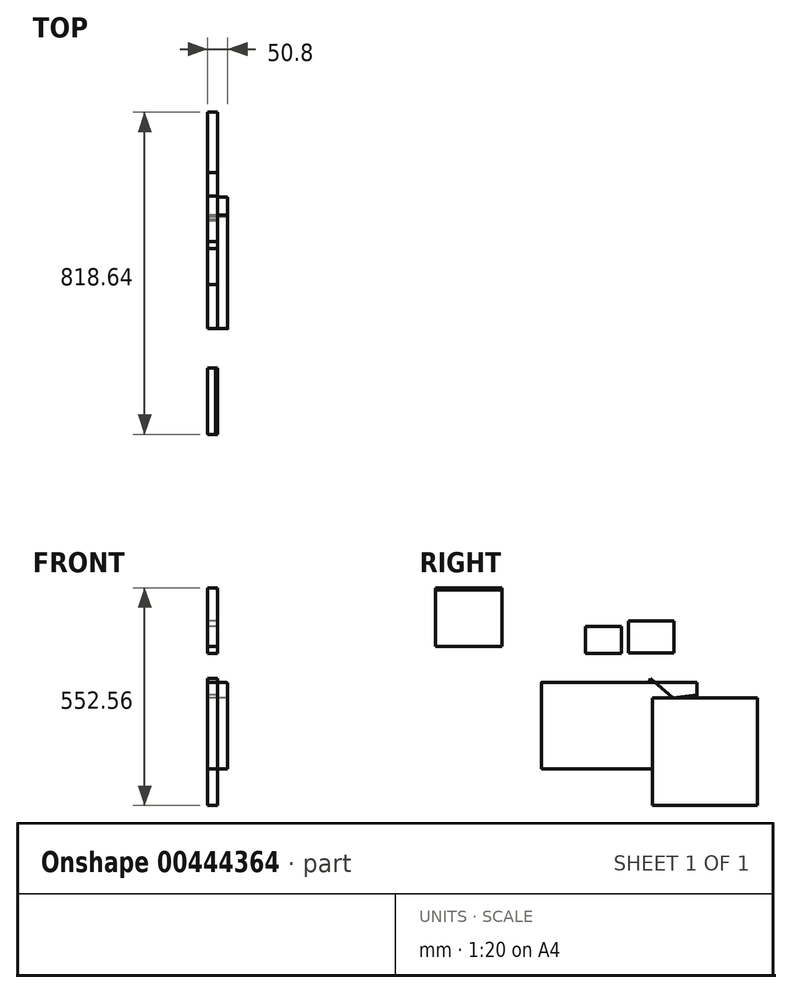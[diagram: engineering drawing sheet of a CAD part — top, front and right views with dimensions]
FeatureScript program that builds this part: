
annotation { "Feature Type Name" : "Feature", "Feature Type Description" : "" }
export const myFeature = defineFeature(function(context is Context, id is Id, definition is map)
    precondition{}
    {
        {
            var Q0;
            Q0=qCreatedBy(makeId("Right.planeOp"),FACE);
            var sketch = newSketch(context, id + "F0", { "sketchPlane" : qUnion([Q0])});
            skLineSegment(sketch, "E0", {"start": v(-200.73, 19.6) * mm, "end": v(-190.85, 48.45) * mm});
            skLineSegment(sketch, "E1", {"start": v(-190.85, 48.45) * mm, "end": v(-133.06, 0) * mm});
            skLineSegment(sketch, "E2", {"start": v(-133.06, 0) * mm, "end": v(122.42, 27.03) * mm});
            skLineSegment(sketch, "E3.bottom", {"start": v(-355.85, 181.44) * mm, "end": v(-264.6, 181.44) * mm});
            skLineSegment(sketch, "E3.top", {"start": v(-355.85, 112.99) * mm, "end": v(-264.6, 112.99) * mm});
            skLineSegment(sketch, "E3.left", {"start": v(-355.85, 181.44) * mm, "end": v(-355.85, 112.99) * mm});
            skLineSegment(sketch, "E3.right", {"start": v(-264.6, 181.44) * mm, "end": v(-264.6, 112.99) * mm});
            skLineSegment(sketch, "E4.bottom", {"start": v(-246.36, 195.26) * mm, "end": v(-130.9, 195.26) * mm});
            skLineSegment(sketch, "E4.top", {"start": v(-246.36, 114.07) * mm, "end": v(-130.9, 114.07) * mm});
            skLineSegment(sketch, "E4.left", {"start": v(-246.36, 195.26) * mm, "end": v(-246.36, 114.07) * mm});
            skLineSegment(sketch, "E4.right", {"start": v(-130.9, 195.26) * mm, "end": v(-130.9, 114.07) * mm});
            skLineSegment(sketch, "E5.bottom", {"start": v(-736.66, 278.99) * mm, "end": v(-567.72, 278.99) * mm});
            skLineSegment(sketch, "E5.top", {"start": v(-736.66, 130.07) * mm, "end": v(-567.72, 130.07) * mm});
            skLineSegment(sketch, "E5.left", {"start": v(-736.66, 278.99) * mm, "end": v(-736.66, 130.07) * mm});
            skLineSegment(sketch, "E5.right", {"start": v(-567.72, 278.99) * mm, "end": v(-567.72, 130.07) * mm});
            skLineSegment(sketch, "E6.bottom", {"start": v(-467.83, 38.79) * mm, "end": v(-71.7, 38.79) * mm});
            skLineSegment(sketch, "E6.top", {"start": v(-467.83, -180.89) * mm, "end": v(-71.7, -180.89) * mm});
            skLineSegment(sketch, "E6.left", {"start": v(-467.83, 38.79) * mm, "end": v(-467.83, -180.89) * mm});
            skLineSegment(sketch, "E6.right", {"start": v(-71.7, 38.79) * mm, "end": v(-71.7, -180.89) * mm});
            skLineSegment(sketch, "E7.bottom", {"start": v(-184.8, 0) * mm, "end": v(81.98, 0) * mm});
            skLineSegment(sketch, "E7.top", {"start": v(-184.8, -273.57) * mm, "end": v(81.98, -273.57) * mm});
            skLineSegment(sketch, "E7.left", {"start": v(-184.8, 0) * mm, "end": v(-184.8, -273.57) * mm});
            skLineSegment(sketch, "E7.right", {"start": v(81.98, 0) * mm, "end": v(81.98, -273.57) * mm});
            skSolve(sketch);
        }
        {
            var Q0;
            {var subQ0=sQuery(id+"F0.wireOp",EDGE,"E6.left");Q0=makeQuery(id+"F0.imprint","IMPRINT",FACE,{"disambiguationData":[TD([[makeQuery(id+"F0.imprint","IMPRINT",EDGE,{"derivedFrom":subQ0}),1.0]])]});}
            extrude(context, id + "F1", {"entities" : qUnion([Q0]), "depth" : 50.8 * mm});
        }
        {
            var Q0;
            Q0=makeQuery(id+"F0.imprint","IMPRINT",FACE,{"disambiguationData":[TD([[makeQuery(id+"F0.imprint","IMPRINT",EDGE,{"derivedFrom":sQuery(id+"F0.wireOp",EDGE,"E3.bottom")}),-1.0]])]});
            var Q1;
            Q1=makeQuery(id+"F0.imprint","IMPRINT",FACE,{"disambiguationData":[TD([[makeQuery(id+"F0.imprint","IMPRINT",EDGE,{"derivedFrom":sQuery(id+"F0.wireOp",EDGE,"E4.bottom")}),-1.0]])]});
            var Q2;
            Q2=makeQuery(id+"F0.imprint","IMPRINT",FACE,{"disambiguationData":[TD([[makeQuery(id+"F0.imprint","IMPRINT",EDGE,{"derivedFrom":sQuery(id+"F0.wireOp",EDGE,"E5.bottom")}),-1.0]])]});
            var Q3;
            {var subQ0=sQuery(id+"F0.wireOp",EDGE,"E1");var subQ1=sQuery(id+"F0.wireOp",EDGE,"E0");var subQ2=makeQuery(id+"F0.imprint","INTERSECT",VERTEX,{"derivedFrom":[subQ1,subQ0]});Q3=makeQuery(id+"F0.imprint","IMPRINT",FACE,{"disambiguationData":[TD([[makeQuery(id+"F0.imprint","IMPRINT",EDGE,{"disambiguationData":[TD([[subQ2,1.0]])],"derivedFrom":subQ1}),-1.0]])]});}
            var Q4;
            {var subQ0=sQuery(id+"F0.wireOp",EDGE,"E2");var subQ1=sQuery(id+"F0.wireOp",EDGE,"E1");var subQ2=makeQuery(id+"F0.imprint","INTERSECT",VERTEX,{"derivedFrom":[subQ1,subQ0]});Q4=makeQuery(id+"F0.imprint","IMPRINT",FACE,{"disambiguationData":[TD([[makeQuery(id+"F0.imprint","IMPRINT",EDGE,{"disambiguationData":[TD([[subQ2,1.0]])],"derivedFrom":subQ1}),1.0]])]});}
            var Q5;
            {var subQ0=sQuery(id+"F0.wireOp",EDGE,"E6.right");var subQ1=sQuery(id+"F0.wireOp",EDGE,"E6.top");var subQ2=makeQuery(id+"F0.imprint","INTERSECT",VERTEX,{"derivedFrom":[subQ1,subQ0]});Q5=makeQuery(id+"F0.imprint","IMPRINT",FACE,{"disambiguationData":[TD([[makeQuery(id+"F0.imprint","IMPRINT",EDGE,{"disambiguationData":[TD([[subQ2,1.0]])],"derivedFrom":subQ1}),1.0]])]});}
            var Q6;
            {var subQ0=sQuery(id+"F0.wireOp",EDGE,"E6.left");Q6=makeQuery(id+"F0.imprint","IMPRINT",FACE,{"disambiguationData":[TD([[makeQuery(id+"F0.imprint","IMPRINT",EDGE,{"derivedFrom":subQ0}),1.0]])]});}
            var Q7;
            {var subQ0=sQuery(id+"F0.wireOp",EDGE,"E7.top");Q7=makeQuery(id+"F0.imprint","IMPRINT",FACE,{"disambiguationData":[TD([[makeQuery(id+"F0.imprint","IMPRINT",EDGE,{"derivedFrom":subQ0}),1.0]])]});}
            extrude(context, id + "F2", {"entities" : qUnion([Q0, Q1, Q2, Q3, Q4, Q5, Q6, Q7]), "operationType" : NewBodyOperationType.ADD, "depth" : 25.4 * mm});
        }
        {
            var Q0;
            Q0 = qSketchRegion(id + "F3Tyac0GpNz8RBf_5", true);
            var Q1;
            Q1 = qSketchRegion(id + "F0", true);
            extrude(context, id + "F3", {"entities" : qUnion([Q0, Q1]), "depth" : 25.4 * mm});
        }
        {
            var Q0;
            Q0=makeQuery(id+"F1.opExtrude","CAP_FACE",FACE,{"disambiguationData":[OSD([sQuery(id+"F0.wireOp",EDGE,"E1"),sQuery(id+"F0.wireOp",EDGE,"E6.bottom"),sQuery(id+"F0.wireOp",EDGE,"E6.top"),sQuery(id+"F0.wireOp",EDGE,"E6.left"),sQuery(id+"F0.wireOp",EDGE,"E7.bottom"),sQuery(id+"F0.wireOp",EDGE,"E7.left")])],"isStart":false});
            var sketch = newSketch(context, id + "F4", { "sketchPlane" : qUnion([Q0])});
            skSolve(sketch);
        }
        {
            var Q0;
            Q0=makeQuery(id+"F1.opExtrude","CAP_EDGE",EDGE,{"disambiguationData":[OSD([sQuery(id+"F0.wireOp",EDGE,"E6.bottom")])],"isStart":false});
            fillet(context, id + "F5", {"entities" : qUnion([Q0]), "radius" : 5.08 * mm, "tangentPropagation" : true, "allowEdgeOverflow" : false});
        }
        {
            var Q0;
            Q0=makeQuery(id+"F2.opExtrude","CAP_EDGE",EDGE,{"disambiguationData":[OSD([sQuery(id+"F0.wireOp",EDGE,"E5.bottom")])],"isStart":false});
            chamfer(context, id + "F6", {"entities" : qUnion([Q0]), "width" : 5.08 * mm, "tangentPropagation" : true});
        }
    });
